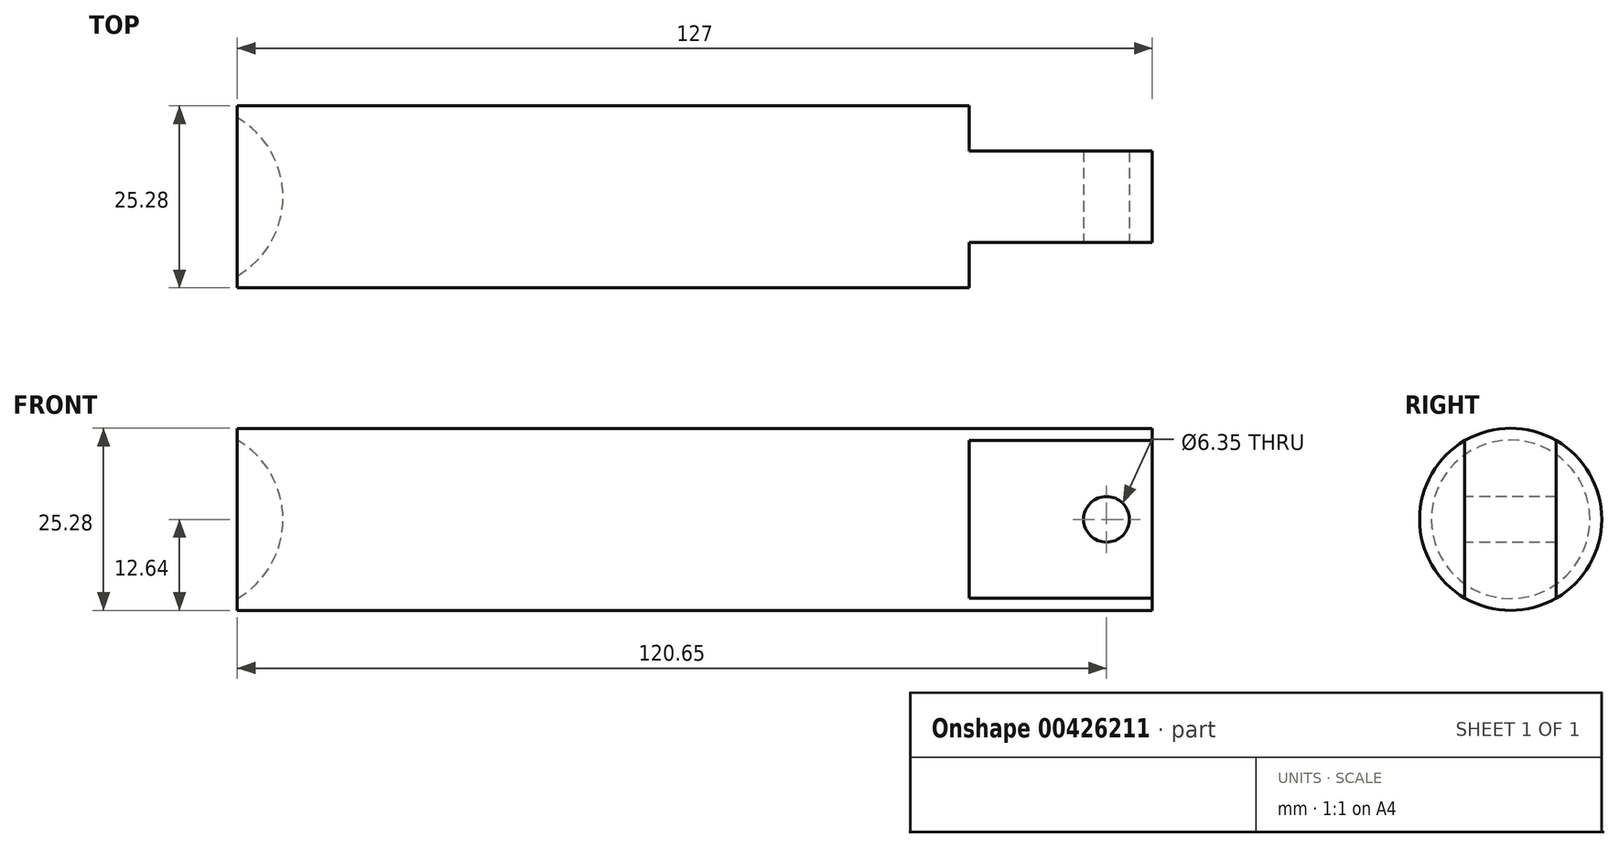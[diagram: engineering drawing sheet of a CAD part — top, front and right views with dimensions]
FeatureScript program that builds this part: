
annotation { "Feature Type Name" : "Feature", "Feature Type Description" : "" }
export const myFeature = defineFeature(function(context is Context, id is Id, definition is map)
    precondition{}
    {
        {
            var Q0;
            Q0=qCreatedBy(makeId("Right.planeOp"),FACE);
            var sketch = newSketch(context, id + "F0", { "sketchPlane" : qUnion([Q0])});
            skCircle(sketch, "E0", {"center": v(0, 0) * mm, "radius": 12.64 * mm});
            skSolve(sketch);
        }
        {
            var Q0;
            Q0 = qSketchRegion(id + "F0", true);
            extrude(context, id + "F1", {"entities" : qUnion([Q0]), "depth" : 127 * mm});
        }
        {
            var Q0;
            Q0=makeQuery(id+"F1.opExtrude","CAP_FACE",FACE,{"disambiguationData":[OSD([sQuery(id+"F0.wireOp",EDGE,"E0")])],"isStart":false});
            var sketch = newSketch(context, id + "F2", { "sketchPlane" : qUnion([Q0])});
            skLineSegment(sketch, "E1.bottom", {"start": v(-6.35, 28.51) * mm, "end": v(-27.24, 28.51) * mm});
            skLineSegment(sketch, "E1.top", {"start": v(-6.35, -25.16) * mm, "end": v(-27.24, -25.16) * mm});
            skLineSegment(sketch, "E1.left", {"start": v(-6.35, 28.51) * mm, "end": v(-6.35, -25.16) * mm});
            skLineSegment(sketch, "E1.right", {"start": v(-27.24, 28.51) * mm, "end": v(-27.24, -25.16) * mm});
            skLineSegment(sketch, "E2.bottom", {"start": v(6.35, 23.18) * mm, "end": v(21.71, 23.18) * mm});
            skLineSegment(sketch, "E2.top", {"start": v(6.35, -29.46) * mm, "end": v(21.71, -29.46) * mm});
            skLineSegment(sketch, "E2.left", {"start": v(6.35, 23.18) * mm, "end": v(6.35, -29.46) * mm});
            skLineSegment(sketch, "E2.right", {"start": v(21.71, 23.18) * mm, "end": v(21.71, -29.46) * mm});
            skSolve(sketch);
        }
        {
            var Q0;
            Q0 = qSketchRegion(id + "F2", true);
            extrude(context, id + "F3", {"entities" : qUnion([Q0]), "operationType" : NewBodyOperationType.REMOVE, "oppositeDirection" : true, "depth" : 25.4 * mm});
        }
        {
            var Q0;
            Q0=qCreatedBy(makeId("Front.planeOp"),FACE);
            var sketch = newSketch(context, id + "F4", { "sketchPlane" : qUnion([Q0])});
            skArc(sketch, "E3", {"start": v(-6.35, -12.7) * mm, "mid": v(6.35, 0) * mm, "end": v(-6.35, 12.7) * mm});
            skLineSegment(sketch, "E4", {"start": v(-6.35, 0) * mm, "end": v(-6.35, 35.91) * mm, "construction": true});
            skLineSegment(sketch, "E5", {"start": v(-6.35, 0) * mm, "end": v(-6.35, -12.7) * mm, "construction": true});
            skLineSegment(sketch, "E6", {"start": v(-6.35, 12.7) * mm, "end": v(-6.35, -12.7) * mm});
            skSolve(sketch);
        }
        {
            var Q0;
            Q0 = qSketchRegion(id + "F4", true);
            var Q1;
            Q1=sQuery(id+"F4.wireOp",EDGE,"E4");
            revolve(context, id + "F5", {"operationType" : NewBodyOperationType.REMOVE, "entities" : qUnion([Q0]), "axis" : qUnion([Q1]), "revolveType" : RevolveType.FULL, "oppositeDirection" : true});
        }
        {
            var Q0;
            Q0=makeQuery(id+"F3.boolean.opBoolean","COPY",FACE,{"derivedFrom":makeQuery(id+"F3.opExtrude","SWEPT_FACE",FACE,{"disambiguationData":[OSD([sQuery(id+"F2.wireOp",EDGE,"E1.left")])]})});
            var sketch = newSketch(context, id + "F6", { "sketchPlane" : qUnion([Q0])});
            skCircle(sketch, "E7", {"center": v(120.65, 0) * mm, "radius": 3.18 * mm});
            skPoint(sketch, "E7.centerSnap0", {"position": v(127, 0) * mm});
            skSolve(sketch);
        }
        {
            var Q0;
            Q0 = qSketchRegion(id + "F6", true);
            extrude(context, id + "F7", {"entities" : qUnion([Q0]), "operationType" : NewBodyOperationType.REMOVE, "endBound" : BoundingType.THROUGH_ALL, "oppositeDirection" : true, "depth" : 25.4 * mm});
        }
    });
